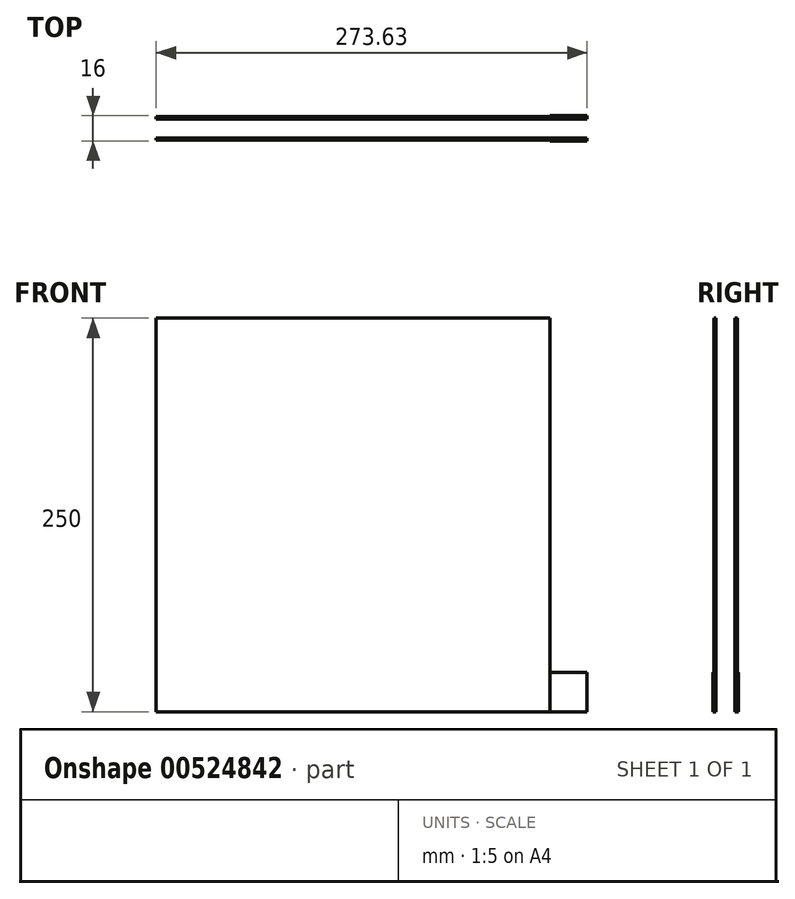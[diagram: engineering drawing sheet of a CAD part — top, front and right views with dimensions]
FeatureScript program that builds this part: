
annotation { "Feature Type Name" : "Feature", "Feature Type Description" : "" }
export const myFeature = defineFeature(function(context is Context, id is Id, definition is map)
    precondition{}
    {
        {
            var Q0;
            Q0=qCreatedBy(makeId("Top.planeOp"),FACE);
            var sketch = newSketch(context, id + "F0", { "sketchPlane" : qUnion([Q0])});
            skLineSegment(sketch, "E0.bottom", {"start": v(-125, 7.5) * mm, "end": v(125, 7.5) * mm});
            skLineSegment(sketch, "E0.top", {"start": v(-125, -7.5) * mm, "end": v(125, -7.5) * mm});
            skLineSegment(sketch, "E0.left", {"start": v(-125, 7.5) * mm, "end": v(-125, -7.5) * mm});
            skLineSegment(sketch, "E0.right", {"start": v(125, 7.5) * mm, "end": v(125, -7.5) * mm});
            skPoint(sketch, "E0.middle", {"position": v(0, 0) * mm});
            skLineSegment(sketch, "E1.bottom", {"start": v(-125, 6) * mm, "end": v(125, 6) * mm});
            skLineSegment(sketch, "E1.top", {"start": v(-125, -6) * mm, "end": v(125, -6) * mm});
            skLineSegment(sketch, "E1.left", {"start": v(-125, 6) * mm, "end": v(-125, -6) * mm});
            skLineSegment(sketch, "E1.right", {"start": v(125, 6) * mm, "end": v(125, -6) * mm});
            skLineSegment(sketch, "E2.bottom", {"start": v(125, -8) * mm, "end": v(148.63, -8) * mm});
            skLineSegment(sketch, "E2.top", {"start": v(125, 8) * mm, "end": v(148.63, 8) * mm});
            skLineSegment(sketch, "E2.left", {"start": v(125, -8) * mm, "end": v(125, 8) * mm});
            skLineSegment(sketch, "E2.right", {"start": v(148.63, -8) * mm, "end": v(148.63, 8) * mm});
            skLineSegment(sketch, "E3", {"start": v(125, 7.5) * mm, "end": v(148.63, 7.5) * mm});
            skLineSegment(sketch, "E4", {"start": v(125, -7.5) * mm, "end": v(148.63, -7.5) * mm});
            skLineSegment(sketch, "E5", {"start": v(148.27, 8) * mm, "end": v(148.63, 8) * mm});
            skLineSegment(sketch, "E6", {"start": v(125, 6) * mm, "end": v(148.63, 6) * mm});
            skLineSegment(sketch, "E7", {"start": v(125, -6) * mm, "end": v(148.63, -6) * mm});
            skSolve(sketch);
        }
        {
            var Q0;
            {var subQ0=sQuery(id+"F0.wireOp",EDGE,"E0.top");Q0=makeQuery(id+"F0.imprint","IMPRINT",FACE,{"disambiguationData":[TD([[makeQuery(id+"F0.imprint","IMPRINT",EDGE,{"derivedFrom":subQ0}),1.0]])]});}
            var Q1;
            {var subQ0=sQuery(id+"F0.wireOp",EDGE,"E0.bottom");Q1=makeQuery(id+"F0.imprint","IMPRINT",FACE,{"disambiguationData":[TD([[makeQuery(id+"F0.imprint","IMPRINT",EDGE,{"derivedFrom":subQ0}),-1.0]])]});}
            extrude(context, id + "F1", {"entities" : qUnion([Q0, Q1]), "depth" : 250 * mm, "offsetDistance" : 25 * mm});
        }
        {
            var Q0;
            {var subQ0=sQuery(id+"F0.wireOp",EDGE,"E3");Q0=makeQuery(id+"F0.imprint","IMPRINT",FACE,{"disambiguationData":[TD([[makeQuery(id+"F0.imprint","IMPRINT",EDGE,{"derivedFrom":subQ0}),-1.0]])]});}
            var Q1;
            {var subQ0=sQuery(id+"F0.wireOp",EDGE,"E4");Q1=makeQuery(id+"F0.imprint","IMPRINT",FACE,{"disambiguationData":[TD([[makeQuery(id+"F0.imprint","IMPRINT",EDGE,{"derivedFrom":subQ0}),1.0]])]});}
            var Q2;
            {var subQ0=sQuery(id+"F0.wireOp",EDGE,"E2.bottom");Q2=makeQuery(id+"F0.imprint","IMPRINT",FACE,{"disambiguationData":[TD([[makeQuery(id+"F0.imprint","IMPRINT",EDGE,{"derivedFrom":subQ0}),1.0]])]});}
            var Q3;
            {var subQ1=sQuery(id+"F0.wireOp",EDGE,"E2.top");Q3=makeQuery(id+"F0.imprint","IMPRINT",FACE,{"disambiguationData":[TD([[makeQuery(id+"F0.imprint","IMPRINT",EDGE,{"derivedFrom":subQ1}),-1.0]])]});}
            extrude(context, id + "F2", {"entities" : qUnion([Q0, Q1, Q2, Q3]), "depth" : 25 * mm, "offsetDistance" : 25 * mm});
        }
    });
